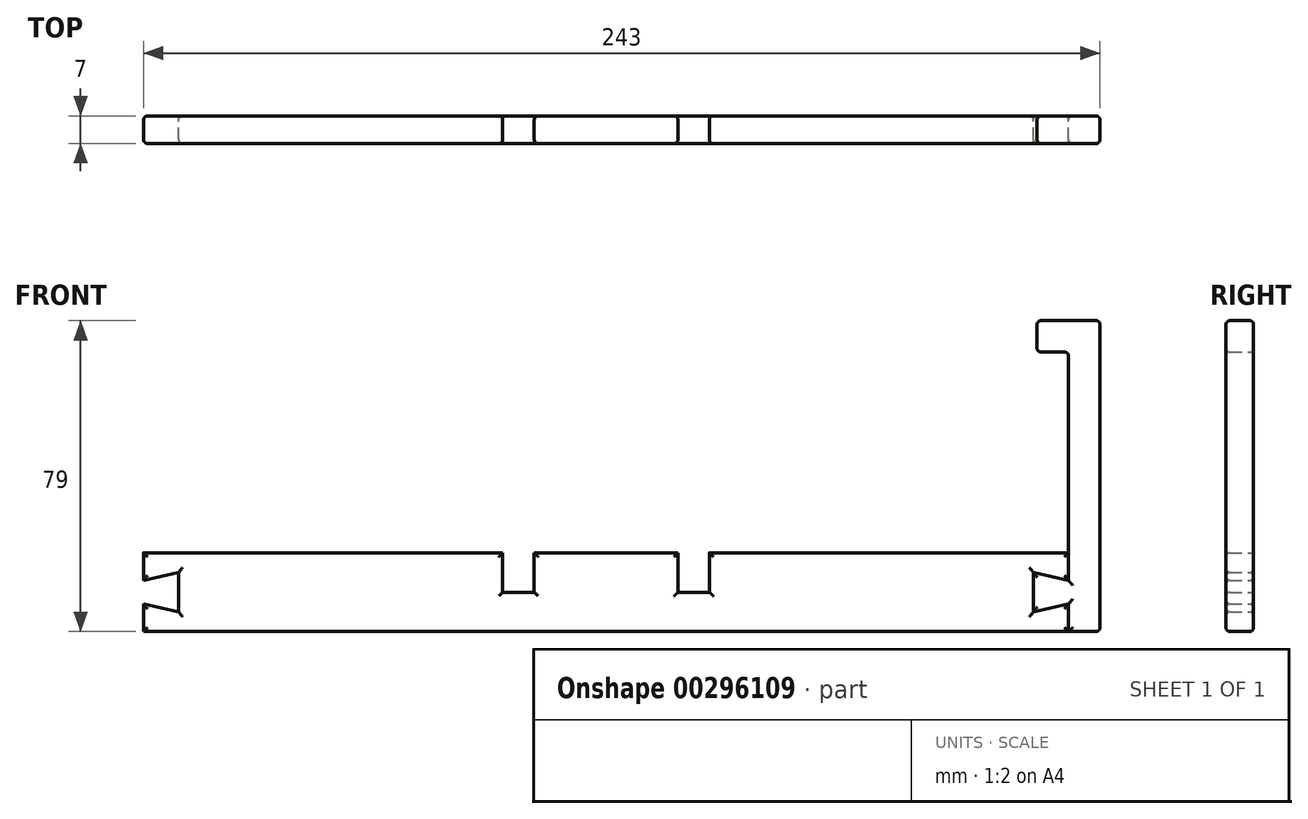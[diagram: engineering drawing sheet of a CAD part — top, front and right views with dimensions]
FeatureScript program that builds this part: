
annotation { "Feature Type Name" : "Feature", "Feature Type Description" : "" }
export const myFeature = defineFeature(function(context is Context, id is Id, definition is map)
    precondition{}
    {
        {
            var Q0;
            Q0=qCreatedBy(makeId("Front.planeOp"),FACE);
            var sketch = newSketch(context, id + "F0", { "sketchPlane" : qUnion([Q0])});
            skLineSegment(sketch, "E0.bottom", {"start": v(117.5, 25.5) * mm, "end": v(-117.5, 25.5) * mm, "construction": true});
            skLineSegment(sketch, "E0.top", {"start": v(117.5, -25.5) * mm, "end": v(-117.5, -25.5) * mm, "construction": true});
            skLineSegment(sketch, "E0.left", {"start": v(117.5, 25.5) * mm, "end": v(117.5, -25.5) * mm, "construction": true});
            skLineSegment(sketch, "E0.right", {"start": v(-117.5, 25.5) * mm, "end": v(-117.5, -25.5) * mm, "construction": true});
            skPoint(sketch, "E0.middle", {"position": v(0, 0) * mm});
            skLineSegment(sketch, "E1", {"start": v(0, -25.5) * mm, "end": v(18.25, -25.5) * mm, "construction": true});
            skLineSegment(sketch, "E2.MirrorCS", {"start": v(0, -25.5) * mm, "end": v(-18.25, -25.5) * mm, "construction": true});
            skLineSegment(sketch, "E3.bottom", {"start": v(-117.5, -25.5) * mm, "end": v(117.5, -25.5) * mm});
            skLineSegment(sketch, "E3.top", {"start": v(-117.5, -45.5) * mm, "end": v(117.5, -45.5) * mm});
            skLineSegment(sketch, "E3.left", {"start": v(-117.5, -25.5) * mm, "end": v(-117.5, -45.5) * mm});
            skLineSegment(sketch, "E3.right", {"start": v(117.5, -25.5) * mm, "end": v(117.5, -45.5) * mm});
            skLineSegment(sketch, "E4.bottom", {"start": v(18.25, -25.5) * mm, "end": v(26.25, -25.5) * mm});
            skLineSegment(sketch, "E4.top", {"start": v(18.25, -35.5) * mm, "end": v(26.25, -35.5) * mm});
            skLineSegment(sketch, "E4.left", {"start": v(18.25, -25.5) * mm, "end": v(18.25, -35.5) * mm});
            skLineSegment(sketch, "E4.right", {"start": v(26.25, -25.5) * mm, "end": v(26.25, -35.5) * mm});
            skLineSegment(sketch, "E5.bottom", {"start": v(117.5, -45.5) * mm, "end": v(125.5, -45.5) * mm});
            skLineSegment(sketch, "E5.top", {"start": v(117.5, 33.5) * mm, "end": v(125.5, 33.5) * mm});
            skLineSegment(sketch, "E5.left", {"start": v(117.5, -45.5) * mm, "end": v(117.5, 33.5) * mm});
            skLineSegment(sketch, "E5.right", {"start": v(125.5, -45.5) * mm, "end": v(125.5, 33.5) * mm});
            skLineSegment(sketch, "E6.bottom", {"start": v(117.5, 33.5) * mm, "end": v(109.5, 33.5) * mm});
            skLineSegment(sketch, "E6.top", {"start": v(117.5, 25.5) * mm, "end": v(109.5, 25.5) * mm});
            skLineSegment(sketch, "E6.left", {"start": v(117.5, 33.5) * mm, "end": v(117.5, 25.5) * mm});
            skLineSegment(sketch, "E6.right", {"start": v(109.5, 33.5) * mm, "end": v(109.5, 25.5) * mm});
            skLineSegment(sketch, "E7.MirrorCS", {"start": v(-117.5, -45.5) * mm, "end": v(-117.5, 33.5) * mm});
            skLineSegment(sketch, "E8.MirrorCS", {"start": v(-125.5, -45.5) * mm, "end": v(-125.5, 33.5) * mm});
            skLineSegment(sketch, "E9.MirrorCS", {"start": v(-117.5, 33.5) * mm, "end": v(-125.5, 33.5) * mm});
            skLineSegment(sketch, "E10.MirrorCS", {"start": v(-117.5, 33.5) * mm, "end": v(-109.5, 33.5) * mm});
            skLineSegment(sketch, "E11.MirrorCS", {"start": v(-109.5, 33.5) * mm, "end": v(-109.5, 25.5) * mm});
            skLineSegment(sketch, "E12.MirrorCS", {"start": v(-117.5, 25.5) * mm, "end": v(-109.5, 25.5) * mm});
            skLineSegment(sketch, "E13.MirrorCS", {"start": v(-117.5, -45.5) * mm, "end": v(-125.5, -45.5) * mm});
            skLineSegment(sketch, "E14.MirrorCS", {"start": v(-18.25, -35.5) * mm, "end": v(-26.25, -35.5) * mm});
            skLineSegment(sketch, "E15.MirrorCS", {"start": v(-18.25, -25.5) * mm, "end": v(-18.25, -35.5) * mm});
            skLineSegment(sketch, "E16.MirrorCS", {"start": v(-26.25, -25.5) * mm, "end": v(-26.25, -35.5) * mm});
            skLineSegment(sketch, "E17", {"start": v(117.5, -45.5) * mm, "end": v(117.5, -38.5) * mm});
            skLineSegment(sketch, "E18", {"start": v(117.5, -38.5) * mm, "end": v(108.59, -40.5) * mm});
            skLineSegment(sketch, "E19", {"start": v(108.59, -40.5) * mm, "end": v(108.59, -30.5) * mm});
            skLineSegment(sketch, "E20", {"start": v(108.59, -30.5) * mm, "end": v(117.5, -32.5) * mm});
            skLineSegment(sketch, "E21", {"start": v(117.5, -32.5) * mm, "end": v(117.5, -25.5) * mm});
            skLineSegment(sketch, "E22", {"start": v(108.59, -30.5) * mm, "end": v(108.59, -25.5) * mm, "construction": true});
            skLineSegment(sketch, "E23", {"start": v(108.59, -40.5) * mm, "end": v(108.59, -45.5) * mm, "construction": true});
            skLineSegment(sketch, "E24.MirrorCS", {"start": v(-117.5, -38.5) * mm, "end": v(-108.59, -40.5) * mm});
            skLineSegment(sketch, "E25.MirrorCS", {"start": v(-108.59, -40.5) * mm, "end": v(-108.59, -30.5) * mm});
            skLineSegment(sketch, "E26.MirrorCS", {"start": v(-108.59, -30.5) * mm, "end": v(-117.5, -32.5) * mm});
            skSolve(sketch);
        }
        {
            var Q0;
            {var subQ6=sQuery(id+"F0.wireOp",EDGE,"E3.top");Q0=makeQuery(id+"F0.imprint","IMPRINT",FACE,{"disambiguationData":[TD([[makeQuery(id+"F0.imprint","IMPRINT",EDGE,{"derivedFrom":subQ6}),1.0]])]});}
            extrude(context, id + "F1", {"entities" : qUnion([Q0]), "depth" : 7 * mm});
        }
        {
            var Q0;
            Q0=makeQuery(id+"F1.opExtrude","CAP_EDGE",EDGE,{"disambiguationData":[OSD([sQuery(id+"F0.wireOp",EDGE,"E3.top")])],"isStart":true});
            var Q1;
            {var subQ0=sQuery(id+"F0.wireOp",EDGE,"E3.bottom");Q1=makeQuery(id+"F1.opExtrude","CAP_EDGE",EDGE,{"disambiguationData":[OSD([subQ0]),TDD([makeQuery(id+"F0.imprint","IMPRINT",EDGE,{"disambiguationData":[TD([[makeQuery(id+"F0.imprint","INTERSECT",VERTEX,{"derivedFrom":[subQ0,sQuery(id+"F0.wireOp",EDGE,"E5.left"),sQuery(id+"F0.wireOp",EDGE,"E21")]}),1.0]])],"derivedFrom":subQ0})])],"isStart":true});}
            var Q2;
            Q2=makeQuery(id+"F1.opExtrude","CAP_EDGE",EDGE,{"disambiguationData":[OSD([sQuery(id+"F0.wireOp",EDGE,"E4.right")])],"isStart":true});
            var Q3;
            Q3=makeQuery(id+"F1.opExtrude","CAP_EDGE",EDGE,{"disambiguationData":[OSD([sQuery(id+"F0.wireOp",EDGE,"E4.top")])],"isStart":true});
            var Q4;
            Q4=makeQuery(id+"F1.opExtrude","CAP_EDGE",EDGE,{"disambiguationData":[OSD([sQuery(id+"F0.wireOp",EDGE,"E4.left")])],"isStart":true});
            var Q5;
            {var subQ0=sQuery(id+"F0.wireOp",EDGE,"E3.bottom");Q5=makeQuery(id+"F1.opExtrude","CAP_EDGE",EDGE,{"disambiguationData":[OSD([subQ0]),TDD([makeQuery(id+"F0.imprint","IMPRINT",EDGE,{"disambiguationData":[TD([[makeQuery(id+"F0.imprint","INTERSECT",VERTEX,{"derivedFrom":[subQ0,sQuery(id+"F0.wireOp",EDGE,"E15.MirrorCS")]}),-1.0]])],"derivedFrom":subQ0})])],"isStart":true});}
            var Q6;
            Q6=makeQuery(id+"F1.opExtrude","CAP_EDGE",EDGE,{"disambiguationData":[OSD([sQuery(id+"F0.wireOp",EDGE,"E15.MirrorCS")])],"isStart":true});
            var Q7;
            Q7=makeQuery(id+"F1.opExtrude","CAP_EDGE",EDGE,{"disambiguationData":[OSD([sQuery(id+"F0.wireOp",EDGE,"E14.MirrorCS")])],"isStart":true});
            var Q8;
            Q8=makeQuery(id+"F1.opExtrude","CAP_EDGE",EDGE,{"disambiguationData":[OSD([sQuery(id+"F0.wireOp",EDGE,"E16.MirrorCS")])],"isStart":true});
            var Q9;
            Q9=makeQuery(id+"F1.opExtrude","CAP_FACE",FACE,{"disambiguationData":[OSD([sQuery(id+"F0.wireOp",EDGE,"E3.bottom"),sQuery(id+"F0.wireOp",EDGE,"E3.top"),sQuery(id+"F0.wireOp",EDGE,"E4.top"),sQuery(id+"F0.wireOp",EDGE,"E4.left"),sQuery(id+"F0.wireOp",EDGE,"E4.right"),sQuery(id+"F0.wireOp",EDGE,"E7.MirrorCS"),sQuery(id+"F0.wireOp",EDGE,"E14.MirrorCS"),sQuery(id+"F0.wireOp",EDGE,"E15.MirrorCS"),sQuery(id+"F0.wireOp",EDGE,"E16.MirrorCS"),sQuery(id+"F0.wireOp",EDGE,"E17"),sQuery(id+"F0.wireOp",EDGE,"E18"),sQuery(id+"F0.wireOp",EDGE,"E19"),sQuery(id+"F0.wireOp",EDGE,"E20"),sQuery(id+"F0.wireOp",EDGE,"E21"),sQuery(id+"F0.wireOp",EDGE,"E24.MirrorCS"),sQuery(id+"F0.wireOp",EDGE,"E25.MirrorCS"),sQuery(id+"F0.wireOp",EDGE,"E26.MirrorCS")])],"isStart":true});
            var Q10;
            Q10=makeQuery(id+"F1.opExtrude","CAP_FACE",FACE,{"disambiguationData":[OSD([sQuery(id+"F0.wireOp",EDGE,"E3.bottom"),sQuery(id+"F0.wireOp",EDGE,"E3.top"),sQuery(id+"F0.wireOp",EDGE,"E4.top"),sQuery(id+"F0.wireOp",EDGE,"E4.left"),sQuery(id+"F0.wireOp",EDGE,"E4.right"),sQuery(id+"F0.wireOp",EDGE,"E7.MirrorCS"),sQuery(id+"F0.wireOp",EDGE,"E14.MirrorCS"),sQuery(id+"F0.wireOp",EDGE,"E15.MirrorCS"),sQuery(id+"F0.wireOp",EDGE,"E16.MirrorCS"),sQuery(id+"F0.wireOp",EDGE,"E17"),sQuery(id+"F0.wireOp",EDGE,"E18"),sQuery(id+"F0.wireOp",EDGE,"E19"),sQuery(id+"F0.wireOp",EDGE,"E20"),sQuery(id+"F0.wireOp",EDGE,"E21"),sQuery(id+"F0.wireOp",EDGE,"E24.MirrorCS"),sQuery(id+"F0.wireOp",EDGE,"E25.MirrorCS"),sQuery(id+"F0.wireOp",EDGE,"E26.MirrorCS")])],"isStart":false});
            var Q11;
            Q11=makeQuery(id+"F1.opExtrude","CAP_EDGE",EDGE,{"disambiguationData":[OSD([sQuery(id+"F0.wireOp",EDGE,"E21")])],"isStart":false});
            fillet(context, id + "F2", {"entities" : qUnion([Q0, Q1, Q2, Q3, Q4, Q5, Q6, Q7, Q8, Q9, Q10, Q11]), "radius" : 1 * mm, "tangentPropagation" : true, "allowEdgeOverflow" : false});
        }
        {
            var Q0;
            Q0=makeQuery(id+"F0.imprint","IMPRINT",FACE,{"disambiguationData":[TD([[makeQuery(id+"F0.imprint","IMPRINT",EDGE,{"derivedFrom":sQuery(id+"F0.wireOp",EDGE,"E5.bottom")}),1.0]])]});
            var Q1;
            {var subQ0=sQuery(id+"F0.wireOp",EDGE,"E18");Q1=makeQuery(id+"F0.imprint","IMPRINT",FACE,{"disambiguationData":[TD([[makeQuery(id+"F0.imprint","IMPRINT",EDGE,{"derivedFrom":subQ0}),-1.0]])]});}
            var Q2;
            Q2=makeQuery(id+"F0.imprint","IMPRINT",FACE,{"disambiguationData":[TD([[makeQuery(id+"F0.imprint","IMPRINT",EDGE,{"derivedFrom":sQuery(id+"F0.wireOp",EDGE,"E6.bottom")}),1.0]])]});
            extrude(context, id + "F3", {"entities" : qUnion([Q0, Q1, Q2]), "depth" : 7 * mm});
        }
        {
            var Q0;
            Q0=makeQuery(id+"F3.opExtrude","CAP_EDGE",EDGE,{"disambiguationData":[OSD([sQuery(id+"F0.wireOp",EDGE,"E5.right")])],"isStart":true});
            var Q1;
            Q1=makeQuery(id+"F3.opExtrude","CAP_FACE",FACE,{"disambiguationData":[OSD([sQuery(id+"F0.wireOp",EDGE,"E5.bottom"),sQuery(id+"F0.wireOp",EDGE,"E5.top"),sQuery(id+"F0.wireOp",EDGE,"E5.left"),sQuery(id+"F0.wireOp",EDGE,"E5.right"),sQuery(id+"F0.wireOp",EDGE,"E6.bottom"),sQuery(id+"F0.wireOp",EDGE,"E6.top"),sQuery(id+"F0.wireOp",EDGE,"E6.right"),sQuery(id+"F0.wireOp",EDGE,"E17"),sQuery(id+"F0.wireOp",EDGE,"E18"),sQuery(id+"F0.wireOp",EDGE,"E19"),sQuery(id+"F0.wireOp",EDGE,"E20"),sQuery(id+"F0.wireOp",EDGE,"E21")])],"isStart":true});
            var Q2;
            Q2=makeQuery(id+"F3.opExtrude","CAP_FACE",FACE,{"disambiguationData":[OSD([sQuery(id+"F0.wireOp",EDGE,"E5.bottom"),sQuery(id+"F0.wireOp",EDGE,"E5.top"),sQuery(id+"F0.wireOp",EDGE,"E5.left"),sQuery(id+"F0.wireOp",EDGE,"E5.right"),sQuery(id+"F0.wireOp",EDGE,"E6.bottom"),sQuery(id+"F0.wireOp",EDGE,"E6.top"),sQuery(id+"F0.wireOp",EDGE,"E6.right"),sQuery(id+"F0.wireOp",EDGE,"E17"),sQuery(id+"F0.wireOp",EDGE,"E18"),sQuery(id+"F0.wireOp",EDGE,"E19"),sQuery(id+"F0.wireOp",EDGE,"E20"),sQuery(id+"F0.wireOp",EDGE,"E21")])],"isStart":false});
            var Q3;
            Q3=makeQuery(id+"F3.opExtrude","SWEPT_FACE",FACE,{"disambiguationData":[OSD([sQuery(id+"F0.wireOp",EDGE,"E5.top"),sQuery(id+"F0.wireOp",EDGE,"E6.bottom")])]});
            var Q4;
            Q4=makeQuery(id+"F3.opExtrude","SWEPT_EDGE",EDGE,{"disambiguationData":[OSD([sQuery(id+"F0.wireOp",EDGE,"E5.bottom"),sQuery(id+"F0.wireOp",EDGE,"E5.right")])]});
            var Q5;
            Q5=makeQuery(id+"F3.opExtrude","SWEPT_FACE",FACE,{"disambiguationData":[OSD([sQuery(id+"F0.wireOp",EDGE,"E6.top")])]});
            fillet(context, id + "F4", {"entities" : qUnion([Q0, Q1, Q2, Q3, Q4, Q5]), "radius" : 1 * mm, "tangentPropagation" : true, "allowEdgeOverflow" : false});
        }
    });
